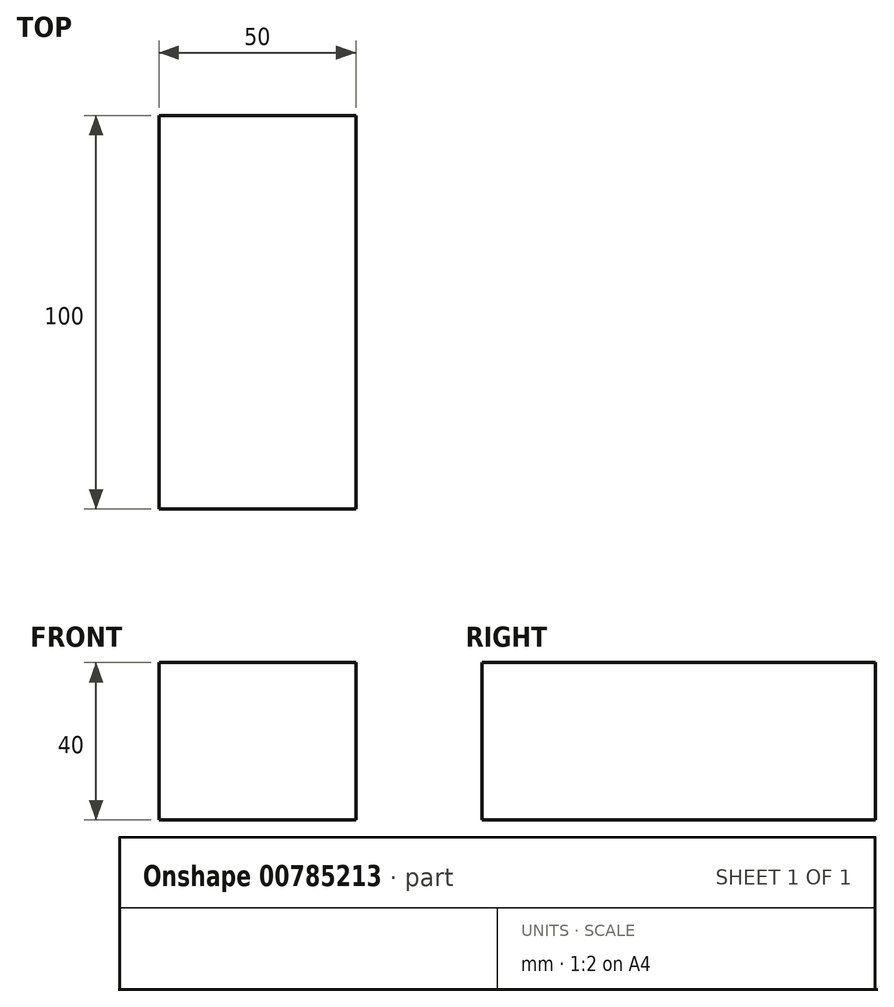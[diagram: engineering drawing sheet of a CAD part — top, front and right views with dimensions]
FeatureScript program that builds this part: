
annotation { "Feature Type Name" : "Feature", "Feature Type Description" : "" }
export const myFeature = defineFeature(function(context is Context, id is Id, definition is map)
    precondition{}
    {
        {
            var Q0;
            Q0=qCreatedBy(makeId("Front.planeOp"),FACE);
            var sketch = newSketch(context, id + "F0", { "sketchPlane" : qUnion([Q0])});
            skLineSegment(sketch, "E0.bottom", {"start": v(0, 0) * mm, "end": v(50, 0) * mm});
            skLineSegment(sketch, "E0.top", {"start": v(0, 40) * mm, "end": v(50, 40) * mm});
            skLineSegment(sketch, "E0.left", {"start": v(0, 0) * mm, "end": v(0, 40) * mm});
            skLineSegment(sketch, "E0.right", {"start": v(50, 0) * mm, "end": v(50, 40) * mm});
            skSolve(sketch);
        }
        {
            var Q0;
            Q0=makeQuery(id+"F0.imprint","IMPRINT",FACE,{"disambiguationData":[TD([[makeQuery(id+"F0.imprint","IMPRINT",EDGE,{"derivedFrom":sQuery(id+"F0.wireOp",EDGE,"E0.bottom")}),1.0]])]});
            extrude(context, id + "F1", {"entities" : qUnion([Q0]), "depth" : 100 * mm, "offsetDistance" : 25 * mm});
        }
    });
